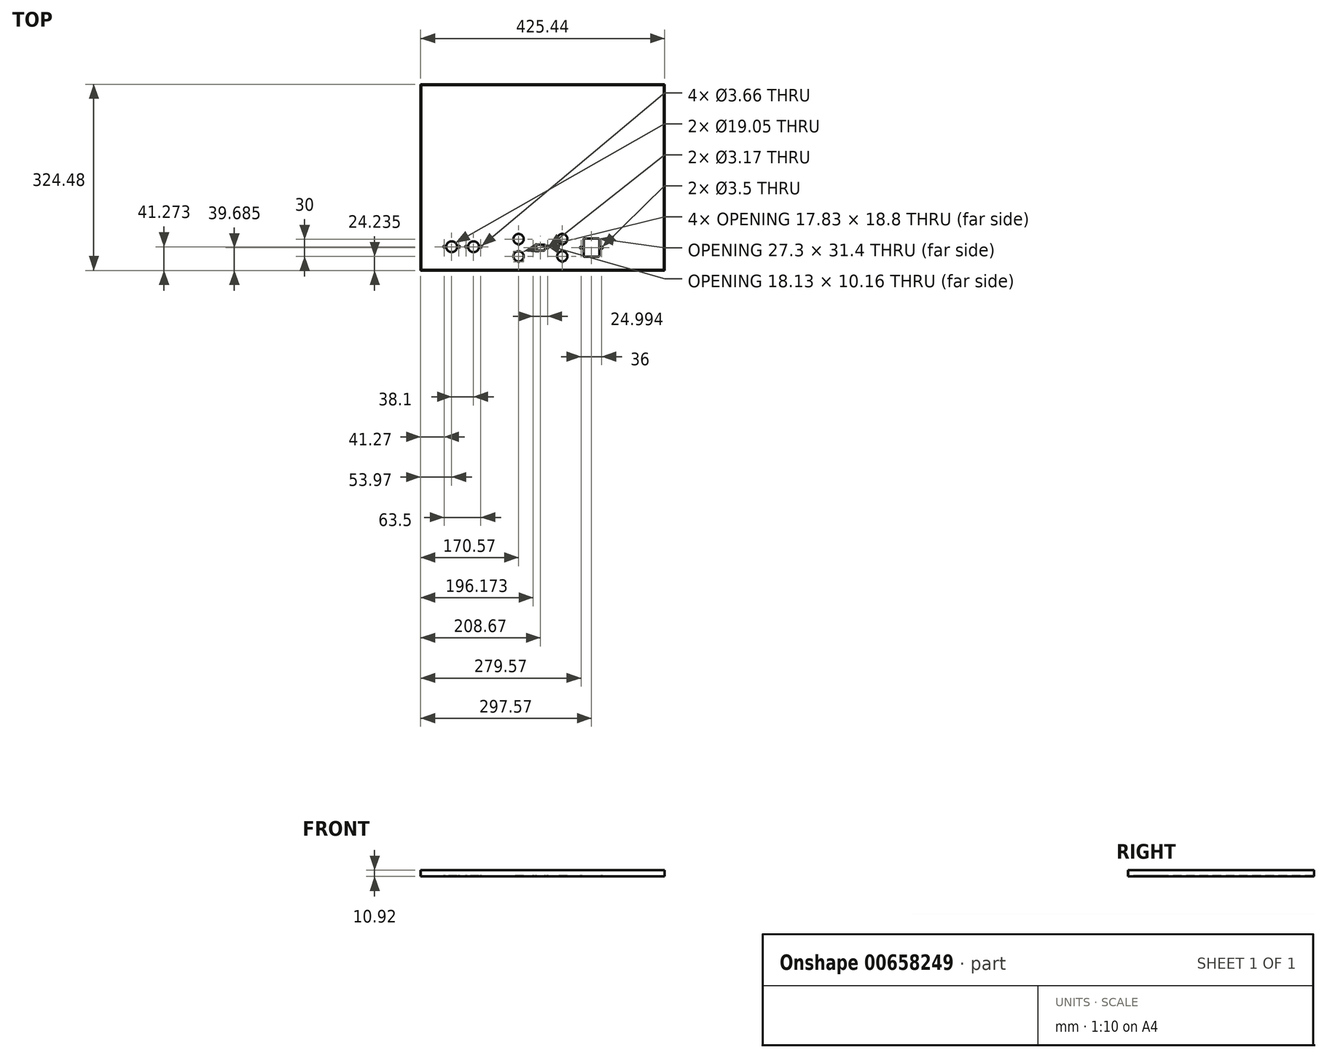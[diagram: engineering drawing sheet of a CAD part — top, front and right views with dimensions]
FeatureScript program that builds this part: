
annotation { "Feature Type Name" : "Feature", "Feature Type Description" : "" }
export const myFeature = defineFeature(function(context is Context, id is Id, definition is map)
    precondition{}
    {
        {
            var Q0;
            Q0=qCreatedBy(makeId("Top.planeOp"),FACE);
            var sketch = newSketch(context, id + "F0", { "sketchPlane" : qUnion([Q0])});
            skLineSegment(sketch, "E0.bottom", {"start": v(-212.73, 162.24) * mm, "end": v(212.73, 162.24) * mm});
            skLineSegment(sketch, "E0.top", {"start": v(-212.73, -162.24) * mm, "end": v(212.72, -162.24) * mm});
            skLineSegment(sketch, "E0.left", {"start": v(-212.72, 162.24) * mm, "end": v(-212.72, -162.24) * mm});
            skLineSegment(sketch, "E0.right", {"start": v(212.73, 162.24) * mm, "end": v(212.73, -162.24) * mm});
            skPoint(sketch, "E1", {"position": v(0, 162.24) * mm});
            skPoint(sketch, "E2", {"position": v(-212.73, 0) * mm});
            skLineSegment(sketch, "E3", {"start": v(-212.72, -82.87) * mm, "end": v(212.72, -82.87) * mm, "construction": true});
            skLineSegment(sketch, "E4", {"start": v(-82.55, -162.24) * mm, "end": v(-82.55, -25.72) * mm, "construction": true});
            skLineSegment(sketch, "E5", {"start": v(-82.55, -25.72) * mm, "end": v(-212.72, -25.72) * mm, "construction": true});
            skLineSegment(sketch, "E6", {"start": v(-57.15, -162.24) * mm, "end": v(-57.15, -25.72) * mm, "construction": true});
            skLineSegment(sketch, "E7", {"start": v(-57.15, -25.72) * mm, "end": v(-82.55, -25.72) * mm, "construction": true});
            skLineSegment(sketch, "E8", {"start": v(-212.72, -120.97) * mm, "end": v(-82.55, -120.97) * mm, "construction": true});
            skPoint(sketch, "E9", {"position": v(-158.75, -120.97) * mm});
            skPoint(sketch, "E10", {"position": v(-120.65, -120.97) * mm});
            skCircle(sketch, "E11", {"center": v(-158.75, -120.97) * mm, "radius": 9.53 * mm});
            skCircle(sketch, "E12", {"center": v(-120.65, -120.97) * mm, "radius": 9.53 * mm});
            skLineSegment(sketch, "E13", {"start": v(-42.15, -82.87) * mm, "end": v(-42.15, -162.24) * mm, "construction": true});
            skArc(sketch, "E14", {"start": v(-40.57, -116.37) * mm, "mid": v(-42.15, -98.6) * mm, "end": v(-43.72, -116.37) * mm});
            skPoint(sketch, "E15", {"position": v(-42.15, -122.55) * mm});
            skArc(sketch, "E16", {"start": v(-40.57, -146.37) * mm, "mid": v(-42.15, -128.6) * mm, "end": v(-43.72, -146.37) * mm});
            skLineSegment(sketch, "E17.top", {"start": v(-43.72, -117.4) * mm, "end": v(-40.57, -117.4) * mm});
            skLineSegment(sketch, "E17.left", {"start": v(-43.72, -116.37) * mm, "end": v(-43.72, -117.4) * mm});
            skLineSegment(sketch, "E17.right", {"start": v(-40.57, -116.37) * mm, "end": v(-40.57, -117.4) * mm});
            skPoint(sketch, "E18", {"position": v(-42.15, -98.6) * mm});
            skLineSegment(sketch, "E19.top", {"start": v(-43.72, -147.4) * mm, "end": v(-40.57, -147.4) * mm});
            skLineSegment(sketch, "E19.left", {"start": v(-43.72, -146.37) * mm, "end": v(-43.72, -147.4) * mm});
            skLineSegment(sketch, "E19.right", {"start": v(-40.57, -146.37) * mm, "end": v(-40.57, -147.4) * mm});
            skPoint(sketch, "E20", {"position": v(-42.15, -128.6) * mm});
            skLineSegment(sketch, "E21", {"start": v(-42.15, -122.55) * mm, "end": v(212.72, -122.56) * mm, "construction": true});
            skLineSegment(sketch, "E22", {"start": v(107.73, -82.87) * mm, "end": v(107.73, -162.24) * mm, "construction": true});
            skPoint(sketch, "E23", {"position": v(-4.05, -122.55) * mm});
            skCircle(sketch, "E24", {"center": v(-16.55, -122.55) * mm, "radius": 1.59 * mm});
            skCircle(sketch, "E25", {"center": v(8.45, -122.55) * mm, "radius": 1.59 * mm});
            skLineSegment(sketch, "E26.bottom", {"start": v(-10.74, -117.47) * mm, "end": v(2.64, -117.47) * mm});
            skLineSegment(sketch, "E26.top", {"start": v(-9.79, -127.63) * mm, "end": v(1.69, -127.63) * mm});
            skPoint(sketch, "E27", {"position": v(-11.08, -122.55) * mm});
            skPoint(sketch, "E28", {"position": v(-4.05, -117.47) * mm});
            skLineSegment(sketch, "E29", {"start": v(-4.05, -122.55) * mm, "end": v(-4.05, -101.32) * mm, "construction": true});
            skLineSegment(sketch, "E30", {"start": v(-13.08, -120.27) * mm, "end": v(-12.13, -125.67) * mm});
            skLineSegment(sketch, "E31", {"start": v(4.98, -120.27) * mm, "end": v(4.03, -125.67) * mm});
            skPoint(sketch, "E32.visualSharp", {"position": v(5.48, -117.47) * mm});
            skArc(sketch, "E32.filletArc", {"start": v(4.98, -120.27) * mm, "mid": v(4.46, -118.33) * mm, "end": v(2.64, -117.47) * mm});
            skPoint(sketch, "E33.visualSharp", {"position": v(3.68, -127.63) * mm});
            skArc(sketch, "E33.filletArc", {"start": v(1.69, -127.64) * mm, "mid": v(3.22, -127.08) * mm, "end": v(4.03, -125.67) * mm});
            skPoint(sketch, "E34.visualSharp", {"position": v(-11.78, -127.63) * mm});
            skArc(sketch, "E34.filletArc", {"start": v(-12.13, -125.67) * mm, "mid": v(-11.32, -127.08) * mm, "end": v(-9.79, -127.64) * mm});
            skPoint(sketch, "E35.visualSharp", {"position": v(-13.57, -117.47) * mm});
            skArc(sketch, "E35.filletArc", {"start": v(-10.74, -117.47) * mm, "mid": v(-12.56, -118.33) * mm, "end": v(-13.08, -120.27) * mm});
            skPoint(sketch, "E36", {"position": v(34.05, -122.55) * mm});
            skLineSegment(sketch, "E37", {"start": v(34.05, -82.87) * mm, "end": v(34.05, -162.24) * mm, "construction": true});
            skArc(sketch, "E38", {"start": v(35.62, -116.37) * mm, "mid": v(34.05, -98.6) * mm, "end": v(32.48, -116.37) * mm});
            skArc(sketch, "E39", {"start": v(35.62, -146.37) * mm, "mid": v(34.05, -128.6) * mm, "end": v(32.48, -146.37) * mm});
            skLineSegment(sketch, "E40.top", {"start": v(32.48, -117.4) * mm, "end": v(35.62, -117.4) * mm});
            skLineSegment(sketch, "E40.left", {"start": v(32.48, -116.37) * mm, "end": v(32.48, -117.4) * mm});
            skLineSegment(sketch, "E40.right", {"start": v(35.62, -116.37) * mm, "end": v(35.62, -117.4) * mm});
            skPoint(sketch, "E41", {"position": v(34.05, -98.6) * mm});
            skPoint(sketch, "E42", {"position": v(32.48, -117.4) * mm});
            skLineSegment(sketch, "E43.top", {"start": v(32.48, -147.4) * mm, "end": v(35.62, -147.4) * mm});
            skLineSegment(sketch, "E43.left", {"start": v(32.48, -146.37) * mm, "end": v(32.48, -147.4) * mm});
            skLineSegment(sketch, "E43.right", {"start": v(35.62, -146.37) * mm, "end": v(35.62, -147.4) * mm});
            skPoint(sketch, "E44", {"position": v(34.05, -128.6) * mm});
            skPoint(sketch, "E45", {"position": v(84.85, -122.56) * mm});
            skLineSegment(sketch, "E46.bottom", {"start": v(72.2, -106.86) * mm, "end": v(97.5, -106.86) * mm});
            skLineSegment(sketch, "E46.top", {"start": v(72.2, -138.26) * mm, "end": v(97.5, -138.26) * mm});
            skLineSegment(sketch, "E46.left", {"start": v(71.2, -107.85) * mm, "end": v(71.2, -137.26) * mm});
            skLineSegment(sketch, "E46.right", {"start": v(98.5, -107.86) * mm, "end": v(98.5, -137.26) * mm});
            skPoint(sketch, "E47", {"position": v(84.85, -106.86) * mm});
            skPoint(sketch, "E48", {"position": v(71.2, -122.55) * mm});
            skLineSegment(sketch, "E49", {"start": v(84.85, -82.87) * mm, "end": v(84.85, -162.24) * mm, "construction": true});
            skCircle(sketch, "E50", {"center": v(66.85, -122.55) * mm, "radius": 1.75 * mm});
            skCircle(sketch, "E51", {"center": v(102.85, -122.56) * mm, "radius": 1.75 * mm});
            skPoint(sketch, "E52.visualSharp", {"position": v(98.5, -106.86) * mm});
            skArc(sketch, "E52.filletArc", {"start": v(98.5, -107.86) * mm, "mid": v(98.2, -107.15) * mm, "end": v(97.5, -106.86) * mm});
            skPoint(sketch, "E53.visualSharp", {"position": v(98.5, -138.25) * mm});
            skArc(sketch, "E53.filletArc", {"start": v(97.5, -138.26) * mm, "mid": v(98.2, -137.96) * mm, "end": v(98.5, -137.26) * mm});
            skPoint(sketch, "E54.visualSharp", {"position": v(71.2, -138.26) * mm});
            skArc(sketch, "E54.filletArc", {"start": v(71.2, -137.26) * mm, "mid": v(71.5, -137.96) * mm, "end": v(72.2, -138.26) * mm});
            skPoint(sketch, "E55.visualSharp", {"position": v(71.2, -106.86) * mm});
            skArc(sketch, "E55.filletArc", {"start": v(72.2, -106.85) * mm, "mid": v(71.5, -107.15) * mm, "end": v(71.2, -107.85) * mm});
            skCircle(sketch, "E56", {"center": v(-171.45, -120.97) * mm, "radius": 1.83 * mm});
            skCircle(sketch, "E57", {"center": v(-146.05, -120.97) * mm, "radius": 1.83 * mm});
            skCircle(sketch, "E58", {"center": v(-133.35, -120.97) * mm, "radius": 1.83 * mm});
            skCircle(sketch, "E59", {"center": v(-107.95, -120.97) * mm, "radius": 1.83 * mm});
            skPoint(sketch, "E60", {"position": v(-42.15, -117.4) * mm});
            skSolve(sketch);
        }
        {
            var Q0;
            Q0=qSketchRegion(id+"F0",true);
            extrude(context, id + "F1", {"entities" : qUnion([Q0]), "depth" : 1.27 * mm, "offsetDistance" : 25.4 * mm});
        }
        {
            var Q0;
            Q0=makeQuery(id+"F1.opExtrude","CAP_FACE",FACE,{"disambiguationData":[OSD([sQuery(id+"F0.wireOp",EDGE,"E0.bottom"),sQuery(id+"F0.wireOp",EDGE,"E0.top"),sQuery(id+"F0.wireOp",EDGE,"E0.left"),sQuery(id+"F0.wireOp",EDGE,"E0.right"),sQuery(id+"F0.wireOp",EDGE,"E11"),sQuery(id+"F0.wireOp",EDGE,"E12"),sQuery(id+"F0.wireOp",EDGE,"E14"),sQuery(id+"F0.wireOp",EDGE,"E16"),sQuery(id+"F0.wireOp",EDGE,"E17.top"),sQuery(id+"F0.wireOp",EDGE,"E17.left"),sQuery(id+"F0.wireOp",EDGE,"E17.right"),sQuery(id+"F0.wireOp",EDGE,"E19.top"),sQuery(id+"F0.wireOp",EDGE,"E19.left"),sQuery(id+"F0.wireOp",EDGE,"E19.right"),sQuery(id+"F0.wireOp",EDGE,"E24"),sQuery(id+"F0.wireOp",EDGE,"E25"),sQuery(id+"F0.wireOp",EDGE,"E26.bottom"),sQuery(id+"F0.wireOp",EDGE,"E26.top"),sQuery(id+"F0.wireOp",EDGE,"E30"),sQuery(id+"F0.wireOp",EDGE,"E31"),sQuery(id+"F0.wireOp",EDGE,"E32.filletArc"),sQuery(id+"F0.wireOp",EDGE,"E33.filletArc"),sQuery(id+"F0.wireOp",EDGE,"E34.filletArc"),sQuery(id+"F0.wireOp",EDGE,"E35.filletArc"),sQuery(id+"F0.wireOp",EDGE,"E38"),sQuery(id+"F0.wireOp",EDGE,"E39"),sQuery(id+"F0.wireOp",EDGE,"E40.top"),sQuery(id+"F0.wireOp",EDGE,"E40.left"),sQuery(id+"F0.wireOp",EDGE,"E40.right"),sQuery(id+"F0.wireOp",EDGE,"E43.top"),sQuery(id+"F0.wireOp",EDGE,"E43.left"),sQuery(id+"F0.wireOp",EDGE,"E43.right"),sQuery(id+"F0.wireOp",EDGE,"E46.bottom"),sQuery(id+"F0.wireOp",EDGE,"E46.top"),sQuery(id+"F0.wireOp",EDGE,"E46.left"),sQuery(id+"F0.wireOp",EDGE,"E46.right"),sQuery(id+"F0.wireOp",EDGE,"E50"),sQuery(id+"F0.wireOp",EDGE,"E51"),sQuery(id+"F0.wireOp",EDGE,"E52.filletArc"),sQuery(id+"F0.wireOp",EDGE,"E53.filletArc"),sQuery(id+"F0.wireOp",EDGE,"E54.filletArc"),sQuery(id+"F0.wireOp",EDGE,"E55.filletArc")])],"isStart":false});
            var sketch = newSketch(context, id + "F2", { "sketchPlane" : qUnion([Q0])});
            skLineSegment(sketch, "E61.bottom", {"start": v(-211.46, 160.97) * mm, "end": v(211.46, 160.97) * mm});
            skLineSegment(sketch, "E61.top", {"start": v(-211.46, -160.97) * mm, "end": v(211.46, -160.97) * mm});
            skLineSegment(sketch, "E61.left", {"start": v(-211.46, 160.97) * mm, "end": v(-211.46, -160.97) * mm});
            skLineSegment(sketch, "E61.right", {"start": v(211.46, 160.97) * mm, "end": v(211.46, -160.97) * mm});
            skLineSegment(sketch, "E62.bottom", {"start": v(-212.73, 162.24) * mm, "end": v(212.73, 162.24) * mm});
            skLineSegment(sketch, "E62.top", {"start": v(-212.73, -162.24) * mm, "end": v(212.73, -162.24) * mm});
            skLineSegment(sketch, "E62.left", {"start": v(-212.73, 162.24) * mm, "end": v(-212.73, -162.24) * mm});
            skLineSegment(sketch, "E62.right", {"start": v(212.73, 162.24) * mm, "end": v(212.73, -162.24) * mm});
            skSolve(sketch);
        }
        {
            var Q0;
            Q0=qSketchRegion(id+"F2",true);
            extrude(context, id + "F3", {"entities" : qUnion([Q0]), "operationType" : NewBodyOperationType.ADD, "depth" : 9.65 * mm, "offsetDistance" : 25.4 * mm});
        }
    });
